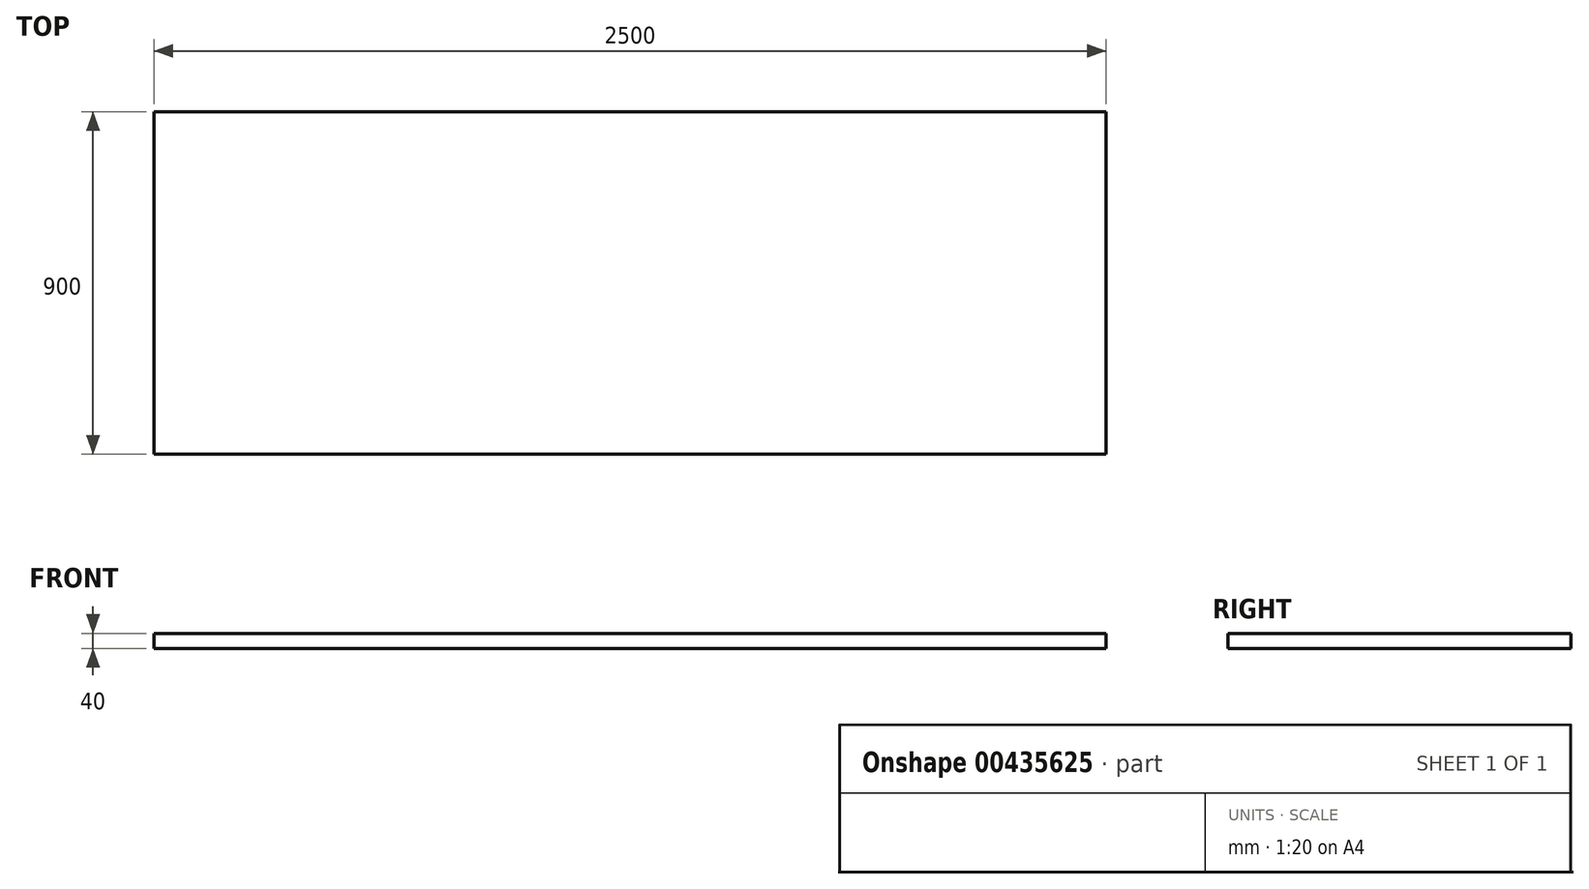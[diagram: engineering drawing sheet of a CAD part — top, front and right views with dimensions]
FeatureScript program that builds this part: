
annotation { "Feature Type Name" : "Feature", "Feature Type Description" : "" }
export const myFeature = defineFeature(function(context is Context, id is Id, definition is map)
    precondition{}
    {
        {
            var Q0;
            Q0=qCreatedBy(makeId("Top.planeOp"),FACE);
            var sketch = newSketch(context, id + "F0", { "sketchPlane" : qUnion([Q0])});
            skLineSegment(sketch, "E0.bottom", {"start": v(-2373.9, 834.5) * mm, "end": v(126.1, 834.5) * mm});
            skLineSegment(sketch, "E0.top", {"start": v(-2373.9, -65.5) * mm, "end": v(126.1, -65.5) * mm});
            skLineSegment(sketch, "E0.left", {"start": v(-2373.9, 834.5) * mm, "end": v(-2373.9, -65.5) * mm});
            skLineSegment(sketch, "E0.right", {"start": v(126.1, 834.5) * mm, "end": v(126.1, -65.5) * mm});
            skLineSegment(sketch, "E1", {"start": v(-2373.9, -65.5) * mm, "end": v(-2373.9, 1383.59) * mm, "construction": true});
            skLineSegment(sketch, "E2", {"start": v(-1868.9, 1402.2) * mm, "end": v(-1868.9, -113.6) * mm, "construction": true});
            skLineSegment(sketch, "E3", {"start": v(-2465.63, 384.5) * mm, "end": v(-1288.51, 384.5) * mm, "construction": true});
            skLineSegment(sketch, "E4", {"start": v(-1868.9, 476.04) * mm, "end": v(-1868.9, 273.77) * mm});
            skLineSegment(sketch, "E5", {"start": v(-1968.38, 384.5) * mm, "end": v(-1793.75, 384.5) * mm});
            skSolve(sketch);
        }
        {
            var Q0;
            Q0 = qSketchRegion(id + "F0", true);
            extrude(context, id + "F1", {"entities" : qUnion([Q0]), "depth" : 40 * mm});
        }
    });
